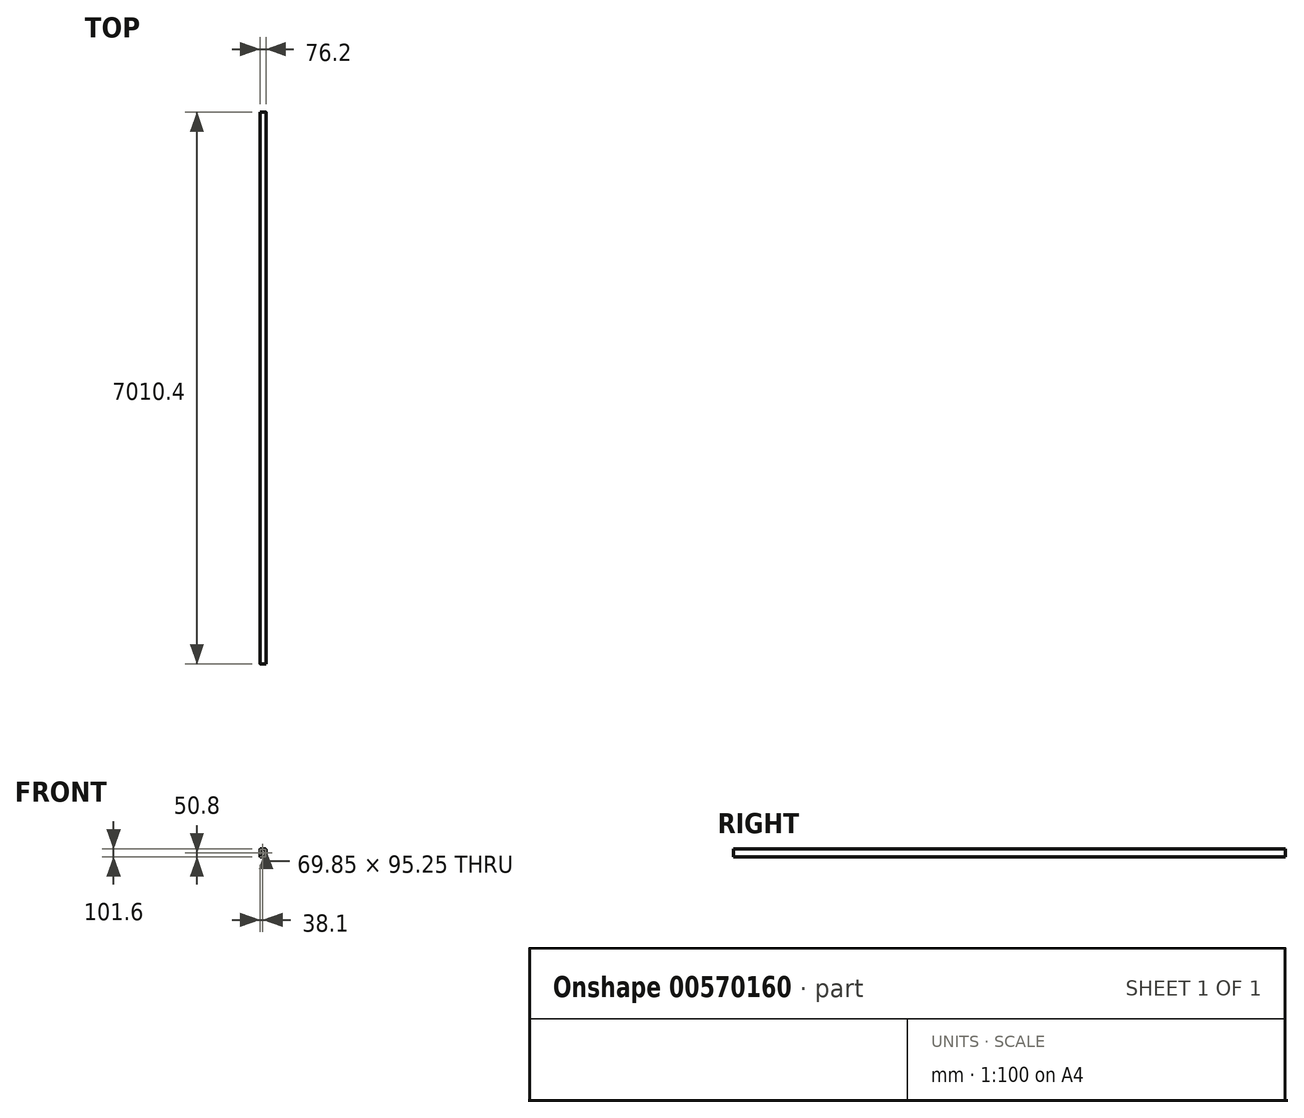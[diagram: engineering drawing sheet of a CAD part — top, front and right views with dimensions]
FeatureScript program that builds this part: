
annotation { "Feature Type Name" : "Feature", "Feature Type Description" : "" }
export const myFeature = defineFeature(function(context is Context, id is Id, definition is map)
    precondition{}
    {
        {
            var Q0;
            Q0=qCreatedBy(makeId("Front.planeOp"),FACE);
            var sketch = newSketch(context, id + "F0", { "sketchPlane" : qUnion([Q0])});
            skLineSegment(sketch, "E0.bottom", {"start": v(0, 0) * mm, "end": v(76.2, 0) * mm});
            skLineSegment(sketch, "E0.top", {"start": v(0, 101.6) * mm, "end": v(76.2, 101.6) * mm});
            skLineSegment(sketch, "E0.left", {"start": v(0, 0) * mm, "end": v(0, 101.6) * mm});
            skLineSegment(sketch, "E0.right", {"start": v(76.2, 0) * mm, "end": v(76.2, 101.6) * mm});
            skLineSegment(sketch, "E1.bottom", {"start": v(73.02, 98.43) * mm, "end": v(3.17, 98.43) * mm});
            skLineSegment(sketch, "E1.top", {"start": v(73.02, 3.18) * mm, "end": v(3.18, 3.17) * mm});
            skLineSegment(sketch, "E1.left", {"start": v(73.02, 98.43) * mm, "end": v(73.03, 3.18) * mm});
            skLineSegment(sketch, "E1.right", {"start": v(3.17, 98.43) * mm, "end": v(3.18, 3.18) * mm});
            skSolve(sketch);
        }
        {
            var Q0;
            Q0=makeQuery(id+"F0.imprint","IMPRINT",FACE,{"disambiguationData":[TD([[makeQuery(id+"F0.imprint","IMPRINT",EDGE,{"derivedFrom":sQuery(id+"F0.wireOp",EDGE,"E0.bottom")}),1.0]])]});
            extrude(context, id + "F1", {"entities" : qUnion([Q0]), "depth" : 7010.4 * mm, "offsetDistance" : 25.4 * mm});
        }
        {
            var Q0;
            Q0=makeQuery(id+"F1.opExtrude","SWEPT_EDGE",EDGE,{"disambiguationData":[OSD([sQuery(id+"F0.wireOp",EDGE,"E0.top"),sQuery(id+"F0.wireOp",EDGE,"E0.left")])]});
            var Q1;
            Q1=makeQuery(id+"F1.opExtrude","SWEPT_EDGE",EDGE,{"disambiguationData":[OSD([sQuery(id+"F0.wireOp",EDGE,"E0.top"),sQuery(id+"F0.wireOp",EDGE,"E0.right")])]});
            var Q2;
            Q2=makeQuery(id+"F1.opExtrude","SWEPT_EDGE",EDGE,{"disambiguationData":[OSD([sQuery(id+"F0.wireOp",EDGE,"E0.bottom"),sQuery(id+"F0.wireOp",EDGE,"E0.left")])]});
            var Q3;
            Q3=makeQuery(id+"F1.opExtrude","SWEPT_EDGE",EDGE,{"disambiguationData":[OSD([sQuery(id+"F0.wireOp",EDGE,"E0.bottom"),sQuery(id+"F0.wireOp",EDGE,"E0.right")])]});
            fillet(context, id + "F2", {"entities" : qUnion([Q0, Q1, Q2, Q3]), "radius" : 5.08 * mm, "tangentPropagation" : true, "allowEdgeOverflow" : false});
        }
    });
